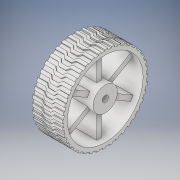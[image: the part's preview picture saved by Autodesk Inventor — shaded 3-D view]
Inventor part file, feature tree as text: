
AUTODESK INVENTOR PART (.ipt)
format: ipt  version: 2019 (Build 230136000, 136)  size: 548,352 bytes
history: native  units: mm
features: extrude x3, sketch x3, other x2, pattern_circular x2
ambient origin geometry x8: Origin, YZ Plane, XZ Plane, XY Plane, X Axis, Y Axis, Z Axis, Center Point
bodies: Body1 (feature_tree), Body2 (feature_tree)
feature tree (10):
  other  "Твердое тело1"
  extrude  "Выдавливание1"  Depth=70.0mm
  extrude  "Выдавливание2"  Depth=4.0mm
  pattern_circular  "Круговой массив1"  Count=2  [1 undecoded]
  other  "РабПлоскость1"
  extrude  "Выдавливание3"  Depth=5.0mm
  pattern_circular  "Круговой массив2"  [2 undecoded]
  sketch  "Эскиз1"
  sketch  "Эскиз2"
  sketch  "Эскиз3"
note: 3 required parameter values undecoded (feature->parameter linkage not recoverable at this tier; creation-order binding heuristic only, values carry confidence <= 0.55)
